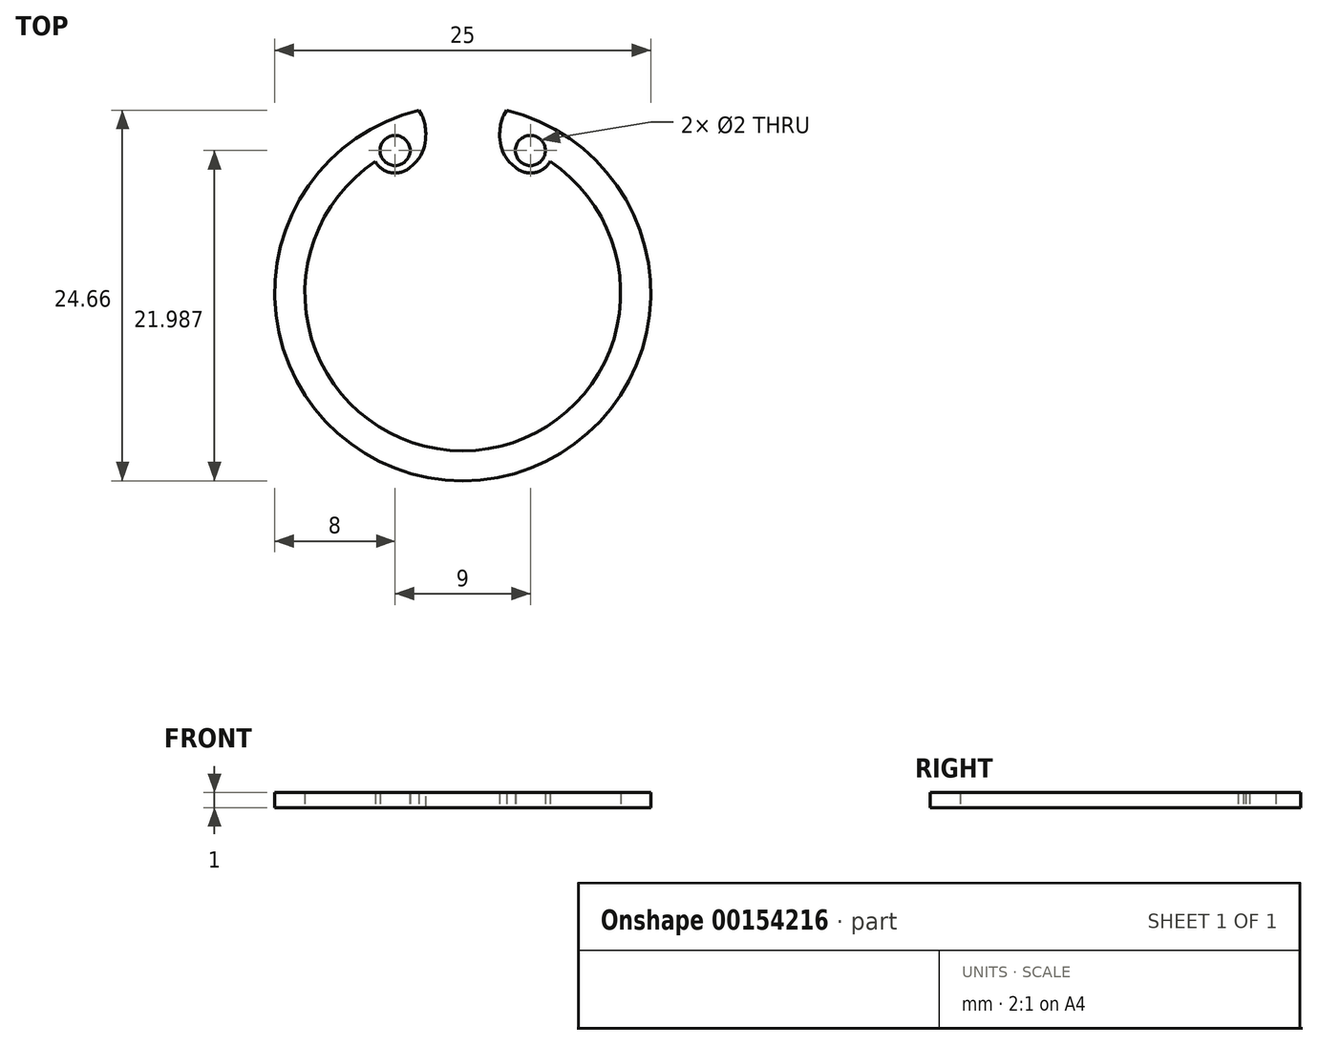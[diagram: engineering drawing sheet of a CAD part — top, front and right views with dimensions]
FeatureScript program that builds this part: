
annotation { "Feature Type Name" : "Feature", "Feature Type Description" : "" }
export const myFeature = defineFeature(function(context is Context, id is Id, definition is map)
    precondition{}
    {
        {
            var Q0;
            Q0=qCreatedBy(makeId("Top.planeOp"),FACE);
            var sketch = newSketch(context, id + "F0", { "sketchPlane" : qUnion([Q0])});
            skArc(sketch, "E0", {"start": v(-2.91, 12.16) * mm, "mid": v(0, -12.5) * mm, "end": v(2.91, 12.16) * mm});
            skArc(sketch, "E1", {"start": v(-5.8, 8.75) * mm, "mid": v(0, -10.5) * mm, "end": v(5.8, 8.75) * mm});
            skLineSegment(sketch, "E2", {"start": v(0, 0) * mm, "end": v(0, 21.24) * mm, "construction": true});
            skCircle(sketch, "E3", {"center": v(-4.5, 9.49) * mm, "radius": 1 * mm});
            skCircle(sketch, "E4.MirrorC", {"center": v(4.5, 9.49) * mm, "radius": 1 * mm});
            skArc(sketch, "E5", {"start": v(-5.8, 8.75) * mm, "mid": v(-4.76, 8) * mm, "end": v(-3.52, 8.35) * mm});
            skArc(sketch, "E6.MirrorC", {"start": v(5.8, 8.75) * mm, "mid": v(4.76, 8) * mm, "end": v(3.52, 8.35) * mm});
            skFitSpline(sketch, "E7", {"points": [v(-2.91, 12.16) * mm, v(-2.5, 11.1) * mm, v(-3.52, 8.35) * mm], "startDerivative": vector(2.34, -3.98) * mm, "endDerivative": vector(-5.77, -4.21) * mm});
            skFitSpline(sketch, "E8.MirrorCS", {"points": [v(2.91, 12.16) * mm, v(2.5, 11.1) * mm, v(3.52, 8.35) * mm], "startDerivative": vector(-2.34, -3.98) * mm, "endDerivative": vector(5.77, -4.21) * mm});
            skSolve(sketch);
        }
        {
            var Q0;
            Q0 = qSketchRegion(id + "F0", true);
            extrude(context, id + "F1", {"entities" : qUnion([Q0]), "depth" : 1 * mm});
        }
    });
